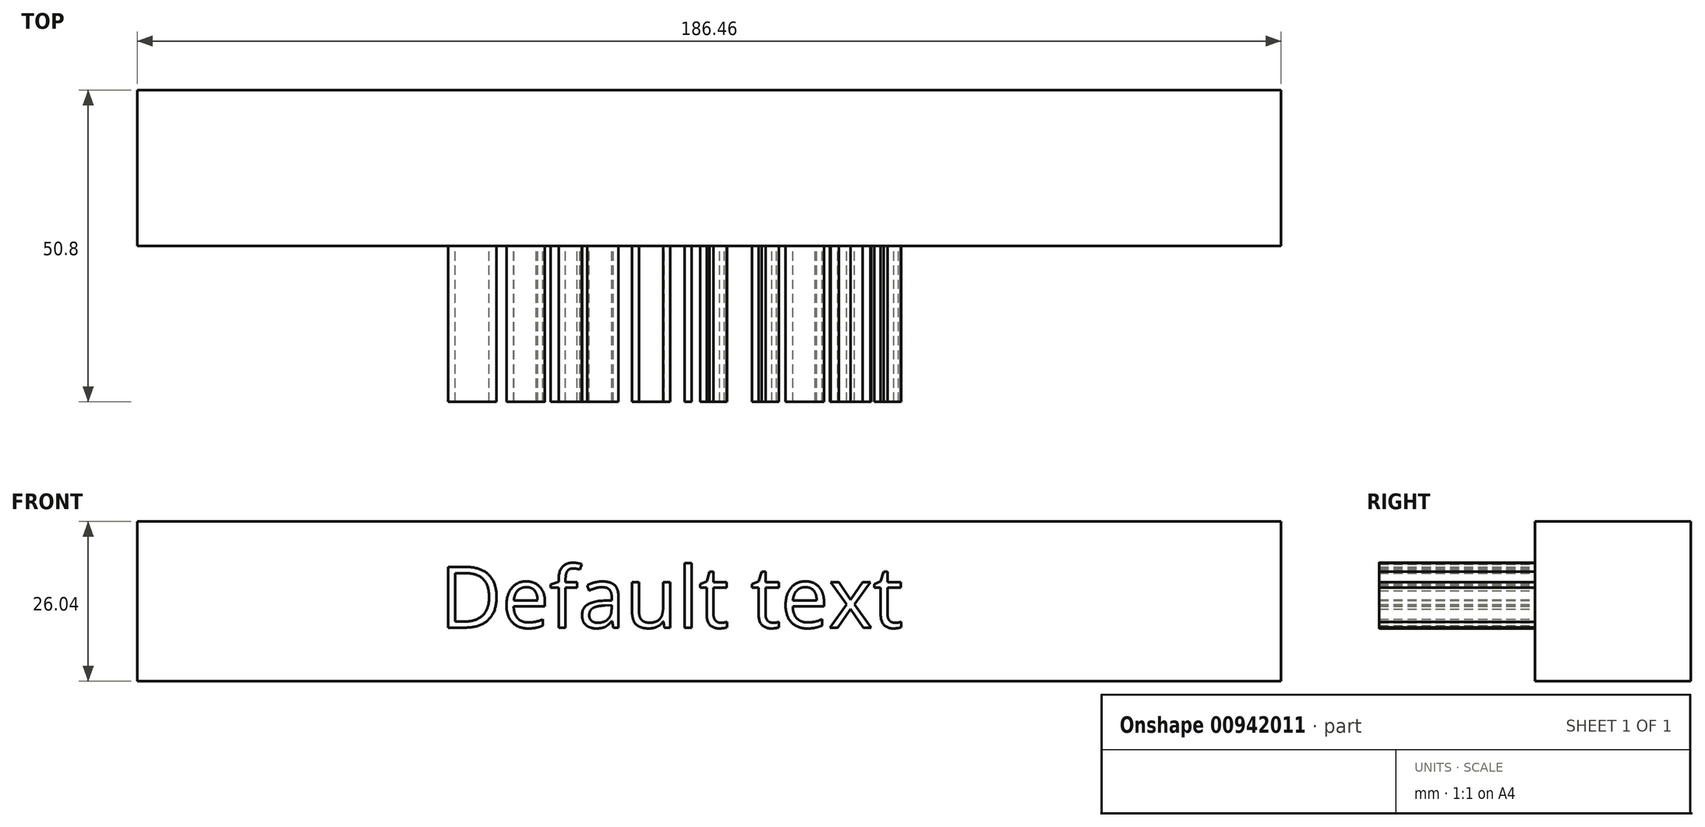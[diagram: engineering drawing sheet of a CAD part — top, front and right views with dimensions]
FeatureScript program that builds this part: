
annotation { "Feature Type Name" : "Feature", "Feature Type Description" : "" }
export const myFeature = defineFeature(function(context is Context, id is Id, definition is map)
    precondition{}
    {
        {
            var Q0;
            Q0=qCreatedBy(makeId("Front.planeOp"),FACE);
            var sketch = newSketch(context, id + "F0", { "sketchPlane" : qUnion([Q0])});
            skLineSegment(sketch, "E0.bottom", {"start": v(-99.91, 53.25) * mm, "end": v(86.55, 53.25) * mm});
            skLineSegment(sketch, "E0.top", {"start": v(-99.91, 27.21) * mm, "end": v(86.55, 27.21) * mm});
            skLineSegment(sketch, "E0.left", {"start": v(-99.91, 53.25) * mm, "end": v(-99.91, 27.21) * mm});
            skLineSegment(sketch, "E0.right", {"start": v(86.55, 53.25) * mm, "end": v(86.55, 27.21) * mm});
            skSolve(sketch);
        }
        {
            var Q0;
            Q0 = qSketchRegion(id + "F0", true);
            extrude(context, id + "F1", {"entities" : qUnion([Q0]), "depth" : 25.4 * mm, "offsetDistance" : 25.4 * mm});
        }
        {
            var Q0;
            Q0=makeQuery(id+"F1.opExtrude","CAP_FACE",FACE,{"disambiguationData":[OSD([sQuery(id+"F0.wireOp",EDGE,"E0.bottom"),sQuery(id+"F0.wireOp",EDGE,"E0.top"),sQuery(id+"F0.wireOp",EDGE,"E0.left"),sQuery(id+"F0.wireOp",EDGE,"E0.right")])],"isStart":false});
            var sketch = newSketch(context, id + "F2", { "sketchPlane" : qUnion([Q0])});
            skText(sketch, "E1", { "text": "Default text", "fontName": "OpenSans-Regular.ttf"});
            const initialGuessF2  = {"E1": [-0.05059, 0.03594, 1, 0, 0.00996]};
            skSetInitialGuess(sketch, initialGuessF2);
            skSolve(sketch);
        }
        {
            var Q0;
            Q0 = qSketchRegion(id + "F2", true);
            extrude(context, id + "F3", {"entities" : qUnion([Q0]), "operationType" : NewBodyOperationType.ADD, "depth" : 25.4 * mm, "offsetDistance" : 25.4 * mm});
        }
    });
